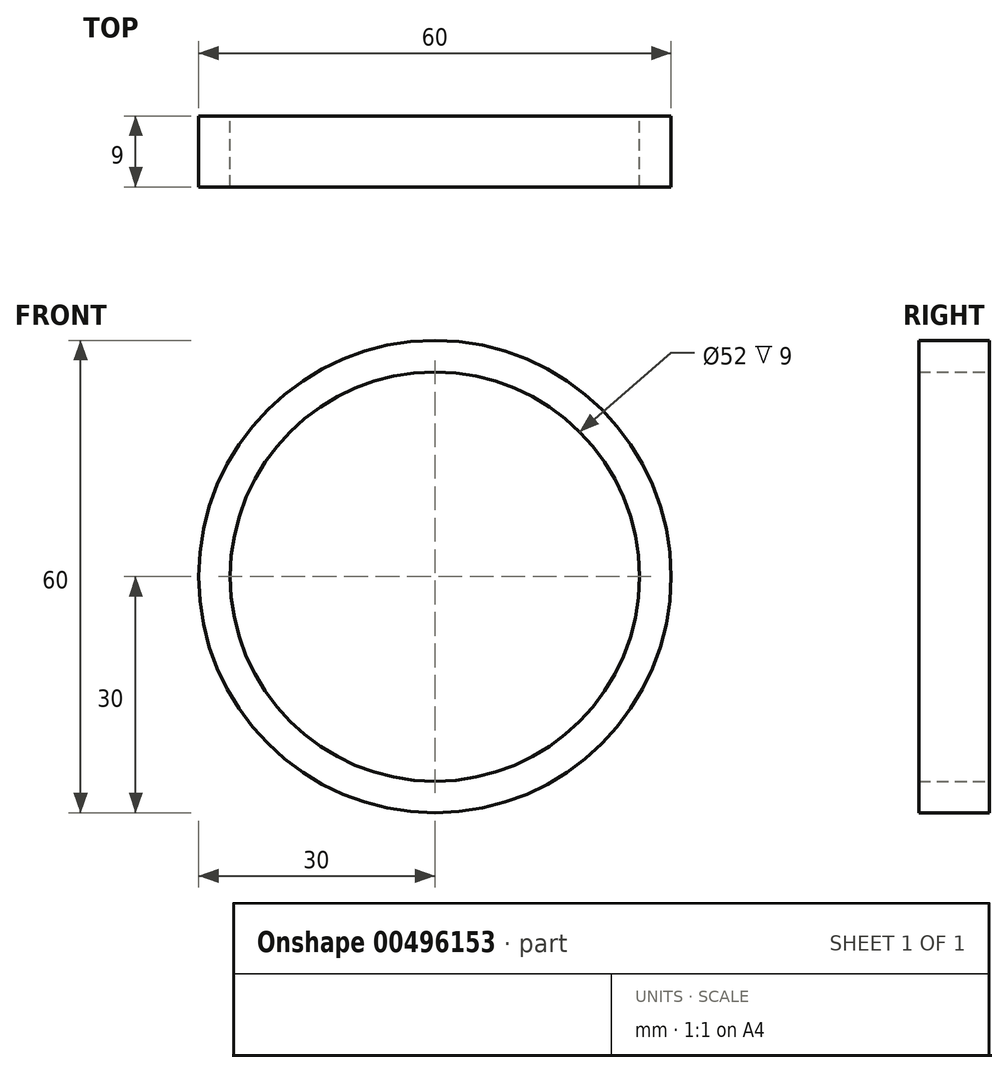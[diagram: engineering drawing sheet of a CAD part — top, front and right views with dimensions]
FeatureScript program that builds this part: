
annotation { "Feature Type Name" : "Feature", "Feature Type Description" : "" }
export const myFeature = defineFeature(function(context is Context, id is Id, definition is map)
    precondition{}
    {
        {
            var Q0;
            Q0=qCreatedBy(makeId("Front.planeOp"),FACE);
            var sketch = newSketch(context, id + "F0", { "sketchPlane" : qUnion([Q0])});
            skCircle(sketch, "E0", {"center": v(0, 0) * mm, "radius": 30 * mm});
            skCircle(sketch, "E1", {"center": v(0, 0) * mm, "radius": 26 * mm});
            skSolve(sketch);
        }
        {
            var Q0;
            Q0 = qSketchRegion(id + "F0", true);
            extrude(context, id + "F1", {"entities" : qUnion([Q0]), "depth" : 9 * mm});
        }
    });
